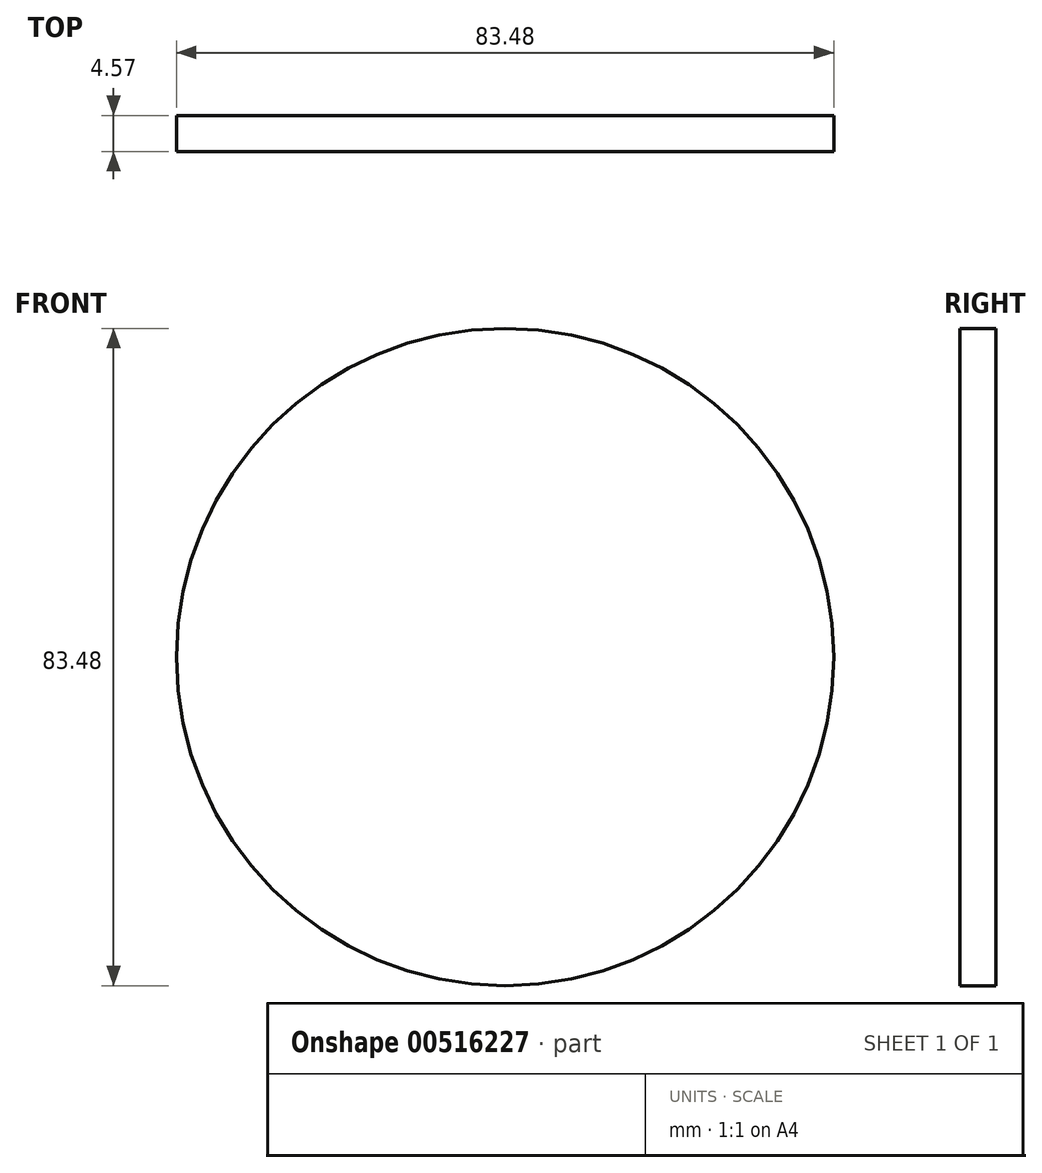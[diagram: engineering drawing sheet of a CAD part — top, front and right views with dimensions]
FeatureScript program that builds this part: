
annotation { "Feature Type Name" : "Feature", "Feature Type Description" : "" }
export const myFeature = defineFeature(function(context is Context, id is Id, definition is map)
    precondition{}
    {
        {
            var Q0;
            Q0=qCreatedBy(makeId("Front.planeOp"),FACE);
            var sketch = newSketch(context, id + "F0", { "sketchPlane" : qUnion([Q0])});
            skCircle(sketch, "E0", {"center": v(0, 0) * mm, "radius": 41.74 * mm});
            skSolve(sketch);
        }
        {
            var Q0;
            Q0 = qSketchRegion(id + "F0", true);
            extrude(context, id + "F1", {"entities" : qUnion([Q0]), "depth" : 4.57 * mm, "offsetDistance" : 25.4 * mm});
        }
    });
